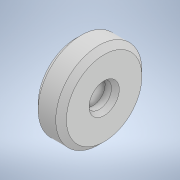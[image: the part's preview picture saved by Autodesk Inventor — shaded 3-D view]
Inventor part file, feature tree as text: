
AUTODESK INVENTOR PART (.ipt)
format: ipt  version: 2022 (Build 260153000, 153)  size: 122,880 bytes
history: native  units: mm
features: sketch x2, other x1, hole x1, projected_geometry x1, revolve x1
ambient origin geometry x8: Origin, YZ Plane, XZ Plane, XY Plane, X Axis, Y Axis, Z Axis, Center Point
bodies: Body1 (feature_tree)
feature tree (6):
  other  "Твердое тело1"
  hole  "Отверстие1"  [1 undecoded]
  sketch  "Эскиз2"
  projected_geometry  "Спроецированная петля1"
  sketch  "Эскиз1"
  revolve  "Вращение1"
note: 1 required parameter value undecoded (feature->parameter linkage not recoverable at this tier; creation-order binding heuristic only, values carry confidence <= 0.55)
